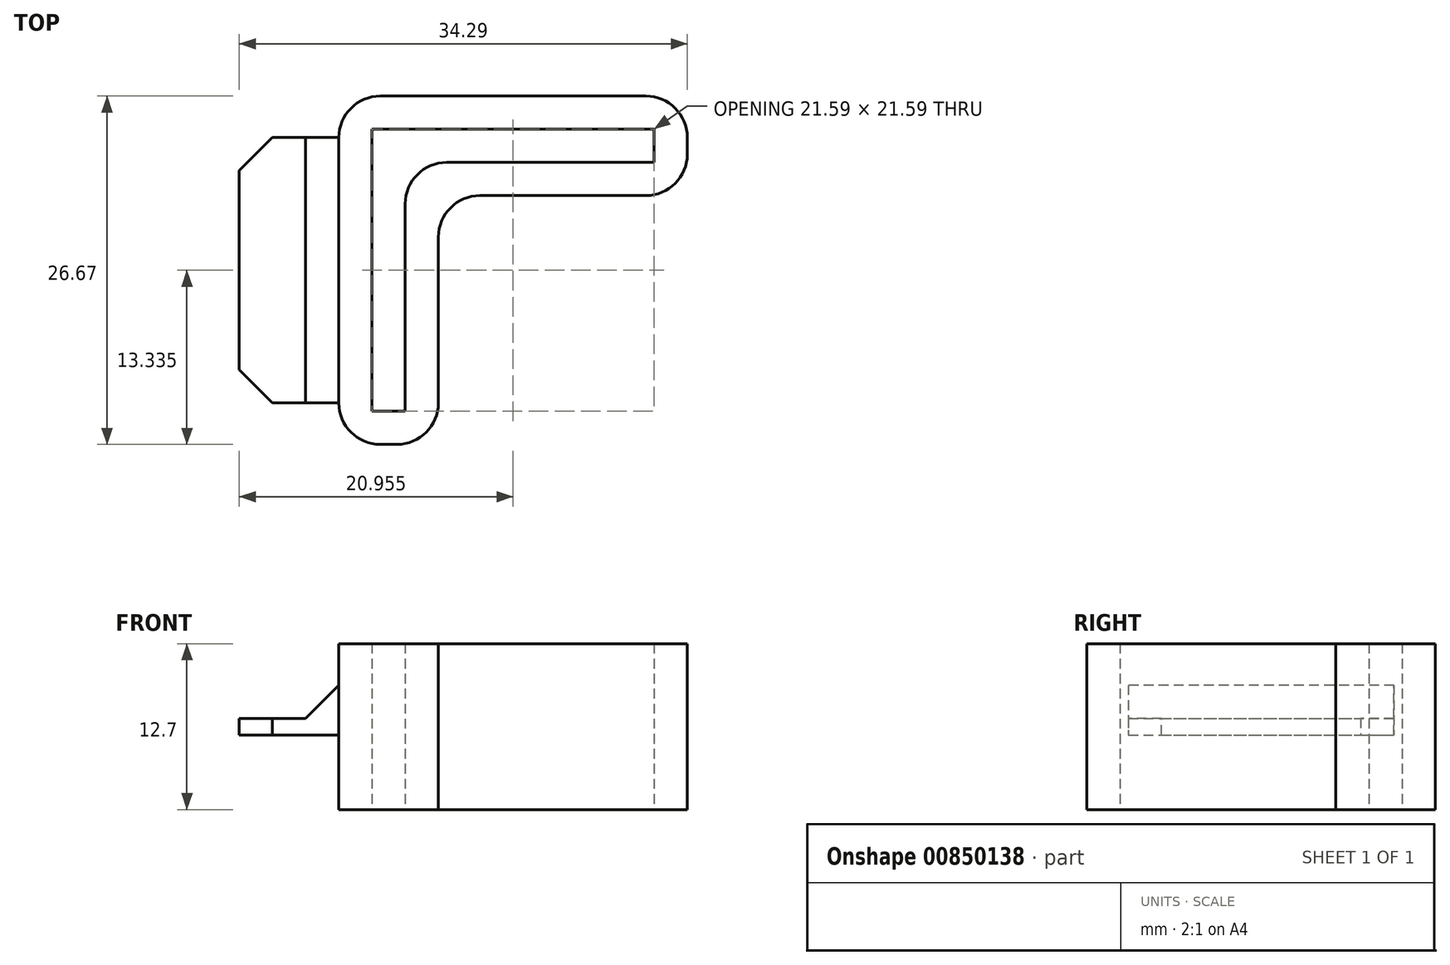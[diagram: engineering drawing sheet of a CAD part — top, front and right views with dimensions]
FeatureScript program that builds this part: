
annotation { "Feature Type Name" : "Feature", "Feature Type Description" : "" }
export const myFeature = defineFeature(function(context is Context, id is Id, definition is map)
    precondition{}
    {
        {
            var Q0;
            Q0=qCreatedBy(makeId("Top.planeOp"),FACE);
            var sketch = newSketch(context, id + "F0", { "sketchPlane" : qUnion([Q0])});
            skLineSegment(sketch, "E0.bottom", {"start": v(2.54, 0) * mm, "end": v(5.08, 0) * mm});
            skLineSegment(sketch, "E0.top", {"start": v(2.54, 21.6) * mm, "end": v(5.08, 21.6) * mm});
            skLineSegment(sketch, "E0.left", {"start": v(2.54, 0) * mm, "end": v(2.54, 21.59) * mm});
            skLineSegment(sketch, "E0.right", {"start": v(5.08, 0) * mm, "end": v(5.08, 19.05) * mm});
            skLineSegment(sketch, "E1.bottom", {"start": v(5.08, 21.6) * mm, "end": v(24.13, 21.6) * mm});
            skLineSegment(sketch, "E1.top", {"start": v(5.08, 19.05) * mm, "end": v(24.13, 19.05) * mm});
            skLineSegment(sketch, "E1.right", {"start": v(24.13, 21.6) * mm, "end": v(24.13, 19.05) * mm});
            skLineSegment(sketch, "E2", {"start": v(0, -2.2) * mm, "end": v(0, 24.13) * mm});
            skLineSegment(sketch, "E3", {"start": v(0, 24.13) * mm, "end": v(26.67, 24.13) * mm});
            skLineSegment(sketch, "E4", {"start": v(26.67, 24.13) * mm, "end": v(26.67, 16.51) * mm});
            skLineSegment(sketch, "E5", {"start": v(26.67, 16.51) * mm, "end": v(7.62, 16.5) * mm});
            skLineSegment(sketch, "E6", {"start": v(7.62, 16.5) * mm, "end": v(7.62, -2.54) * mm});
            skLineSegment(sketch, "E7", {"start": v(7.62, -2.54) * mm, "end": v(0, -2.54) * mm});
            skLineSegment(sketch, "E8", {"start": v(0, -2.54) * mm, "end": v(0, -2.2) * mm});
            skSolve(sketch);
        }
        {
            var Q0;
            Q0 = qSketchRegion(id + "F0", true);
            extrude(context, id + "F1", {"entities" : qUnion([Q0]), "depth" : 12.7 * mm, "offsetDistance" : 25.4 * mm});
        }
        {
            var Q0;
            Q0=makeQuery(id+"F1.opExtrude","SWEPT_EDGE",EDGE,{"disambiguationData":[OSD([sQuery(id+"F0.wireOp",EDGE,"E3"),sQuery(id+"F0.wireOp",EDGE,"E4")])]});
            var Q1;
            Q1=makeQuery(id+"F1.opExtrude","SWEPT_EDGE",EDGE,{"disambiguationData":[OSD([sQuery(id+"F0.wireOp",EDGE,"E4"),sQuery(id+"F0.wireOp",EDGE,"E5")])]});
            var Q2;
            Q2=makeQuery(id+"F1.opExtrude","SWEPT_EDGE",EDGE,{"disambiguationData":[OSD([sQuery(id+"F0.wireOp",EDGE,"E0.right"),sQuery(id+"F0.wireOp",EDGE,"E1.top")])]});
            var Q3;
            Q3=makeQuery(id+"F1.opExtrude","SWEPT_EDGE",EDGE,{"disambiguationData":[OSD([sQuery(id+"F0.wireOp",EDGE,"E2"),sQuery(id+"F0.wireOp",EDGE,"E3")])]});
            var Q4;
            Q4=makeQuery(id+"F1.opExtrude","SWEPT_EDGE",EDGE,{"disambiguationData":[OSD([sQuery(id+"F0.wireOp",EDGE,"E6"),sQuery(id+"F0.wireOp",EDGE,"E7")])]});
            var Q5;
            Q5=makeQuery(id+"F1.opExtrude","SWEPT_EDGE",EDGE,{"disambiguationData":[OSD([sQuery(id+"F0.wireOp",EDGE,"E7"),sQuery(id+"F0.wireOp",EDGE,"E8")])]});
            var Q6;
            Q6=makeQuery(id+"F1.opExtrude","SWEPT_EDGE",EDGE,{"disambiguationData":[OSD([sQuery(id+"F0.wireOp",EDGE,"E5"),sQuery(id+"F0.wireOp",EDGE,"E6")])]});
            fillet(context, id + "F2", {"entities" : qUnion([Q0, Q1, Q2, Q3, Q4, Q5, Q6]), "radius" : 3.17 * mm, "tangentPropagation" : true, "allowEdgeOverflow" : false});
        }
        {
            var Q0;
            Q0=makeQuery(id+"F1.opExtrude","SWEPT_FACE",FACE,{"disambiguationData":[OSD([sQuery(id+"F0.wireOp",EDGE,"E2"),sQuery(id+"F0.wireOp",EDGE,"E8")])]});
            var sketch = newSketch(context, id + "F3", { "sketchPlane" : qUnion([Q0])});
            skLineSegment(sketch, "E9.bottom", {"start": v(-0.63, 5.71) * mm, "end": v(-20.96, 5.71) * mm});
            skLineSegment(sketch, "E9.top", {"start": v(-0.63, 6.99) * mm, "end": v(-20.96, 6.99) * mm});
            skLineSegment(sketch, "E9.left", {"start": v(-0.63, 5.71) * mm, "end": v(-0.63, 6.99) * mm});
            skLineSegment(sketch, "E9.right", {"start": v(-20.96, 5.71) * mm, "end": v(-20.96, 6.99) * mm});
            skSolve(sketch);
        }
        {
            var Q0;
            Q0 = qSketchRegion(id + "F3", true);
            extrude(context, id + "F4", {"entities" : qUnion([Q0]), "operationType" : NewBodyOperationType.ADD, "depth" : 7.62 * mm, "offsetDistance" : 25.4 * mm});
        }
        {
            var Q0;
            Q0=makeQuery(id+"F4.opExtrude","CAP_EDGE",EDGE,{"disambiguationData":[OSD([sQuery(id+"F3.wireOp",EDGE,"E9.bottom")])],"isStart":true});
            var Q1;
            Q1=makeQuery(id+"F4.opExtrude","CAP_EDGE",EDGE,{"disambiguationData":[OSD([sQuery(id+"F3.wireOp",EDGE,"E9.top")])],"isStart":true});
            var Q2;
            Q2=makeQuery(id+"F4.opExtrude","CAP_EDGE",EDGE,{"disambiguationData":[OSD([sQuery(id+"F3.wireOp",EDGE,"E9.right")])],"isStart":false});
            var Q3;
            Q3=makeQuery(id+"F4.opExtrude","CAP_EDGE",EDGE,{"disambiguationData":[OSD([sQuery(id+"F3.wireOp",EDGE,"E9.left")])],"isStart":false});
            chamfer(context, id + "F5", {"entities" : qUnion([Q0, Q1, Q2, Q3]), "width" : 2.54 * mm, "tangentPropagation" : true});
        }
    });
